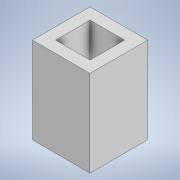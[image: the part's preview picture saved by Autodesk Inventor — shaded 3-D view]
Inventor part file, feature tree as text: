
AUTODESK INVENTOR PART (.ipt)
format: ipt  version: 2022 (Build 260153000, 153)  size: 95,744 bytes
history: native  units: in
note: dims shown in document units (in); Inventor stores cm internally (conversion verified against a paired STEP export)
features: extrude x1, shell x1, sketch x1
ambient origin geometry x8: Origin, YZ Plane, XZ Plane, XY Plane, X Axis, Y Axis, Z Axis, Center Point
bodies: Solid1 (feature_tree)
feature tree (3):
  extrude  "Extrusion1"  Depth=0.1969in
  shell  "Shell1"  Thickness=0.2953in
  sketch  "Sketch1"  dims[d0=0.1969in d1=0.1969in d2=0.2953in d3=0.0in d4=0.0394in]
